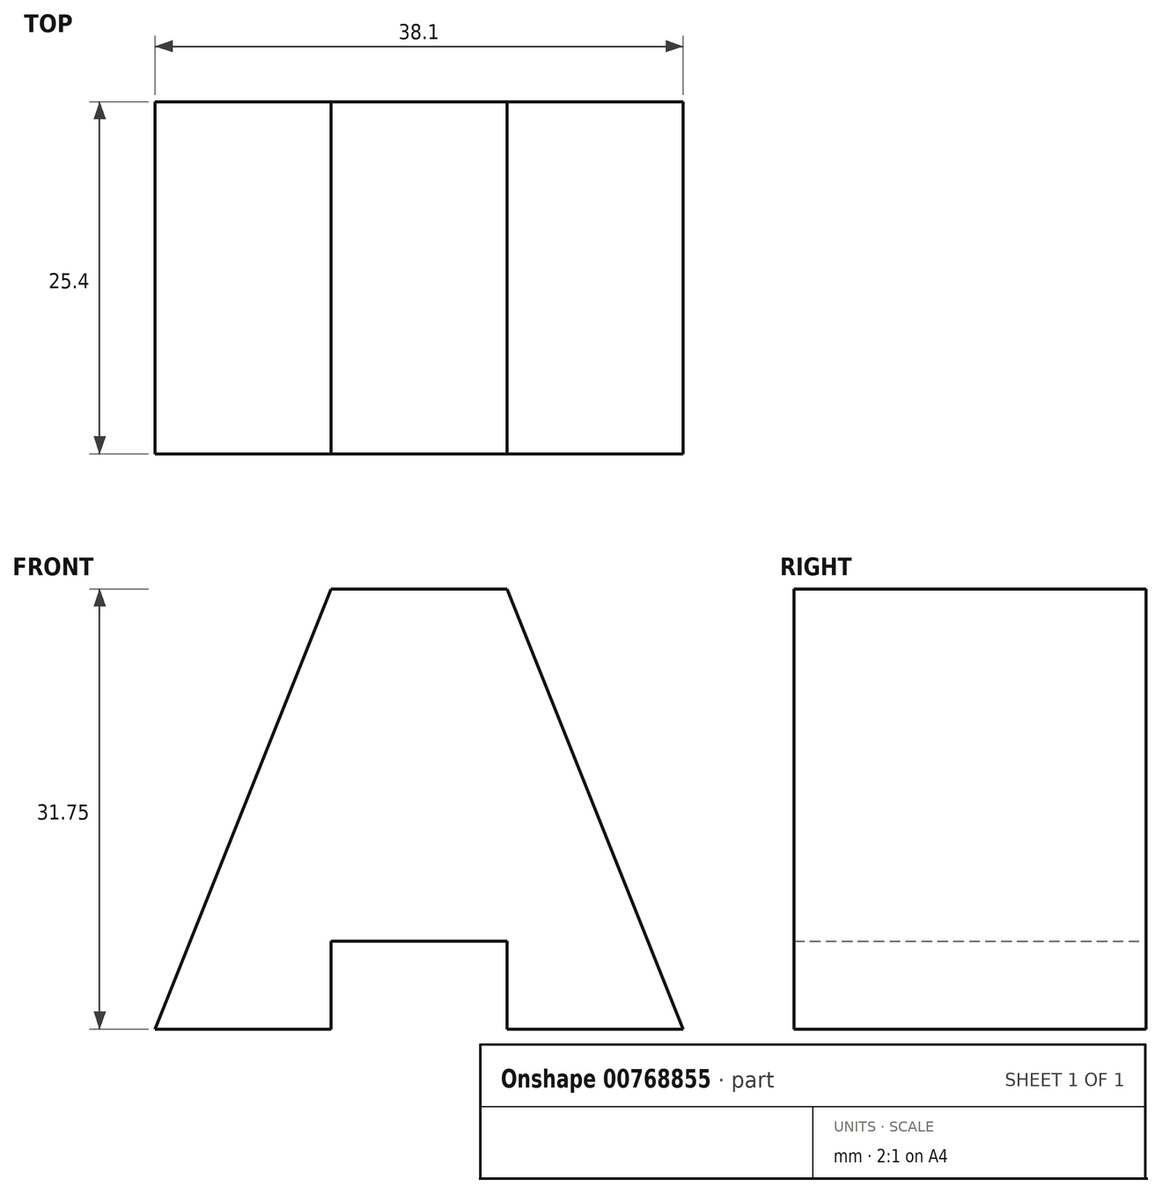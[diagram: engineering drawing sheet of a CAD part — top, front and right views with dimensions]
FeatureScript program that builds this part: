
annotation { "Feature Type Name" : "Feature", "Feature Type Description" : "" }
export const myFeature = defineFeature(function(context is Context, id is Id, definition is map)
    precondition{}
    {
        {
            var Q0;
            Q0=qCreatedBy(makeId("Front.planeOp"),FACE);
            var sketch = newSketch(context, id + "F0", { "sketchPlane" : qUnion([Q0])});
            skLineSegment(sketch, "E0", {"start": v(0, 0) * mm, "end": v(12.7, 0) * mm});
            skLineSegment(sketch, "E1", {"start": v(12.7, 0) * mm, "end": v(12.7, 6.35) * mm});
            skLineSegment(sketch, "E2", {"start": v(12.7, 6.35) * mm, "end": v(25.4, 6.35) * mm});
            skLineSegment(sketch, "E3", {"start": v(25.4, 6.35) * mm, "end": v(25.4, 0) * mm});
            skLineSegment(sketch, "E4", {"start": v(25.4, 0) * mm, "end": v(38.1, 0) * mm});
            skLineSegment(sketch, "E5", {"start": v(25.4, 6.35) * mm, "end": v(25.4, 31.75) * mm});
            skLineSegment(sketch, "E6", {"start": v(25.4, 31.75) * mm, "end": v(38.1, 0) * mm});
            skLineSegment(sketch, "E7", {"start": v(25.4, 31.75) * mm, "end": v(12.7, 31.75) * mm});
            skLineSegment(sketch, "E8", {"start": v(12.7, 31.75) * mm, "end": v(0, 0) * mm});
            skSolve(sketch);
        }
        {
            var Q0;
            Q0=makeQuery(id+"F0.imprint","IMPRINT",FACE,{"disambiguationData":[TD([[makeQuery(id+"F0.imprint","IMPRINT",EDGE,{"derivedFrom":sQuery(id+"F0.wireOp",EDGE,"E0")}),1.0]])]});
            var Q1;
            Q1=makeQuery(id+"F0.imprint","IMPRINT",FACE,{"disambiguationData":[TD([[makeQuery(id+"F0.imprint","IMPRINT",EDGE,{"derivedFrom":sQuery(id+"F0.wireOp",EDGE,"E3")}),1.0]])]});
            extrude(context, id + "F1", {"entities" : qUnion([Q0, Q1]), "depth" : 25.4 * mm, "offsetDistance" : 25.4 * mm});
        }
    });
